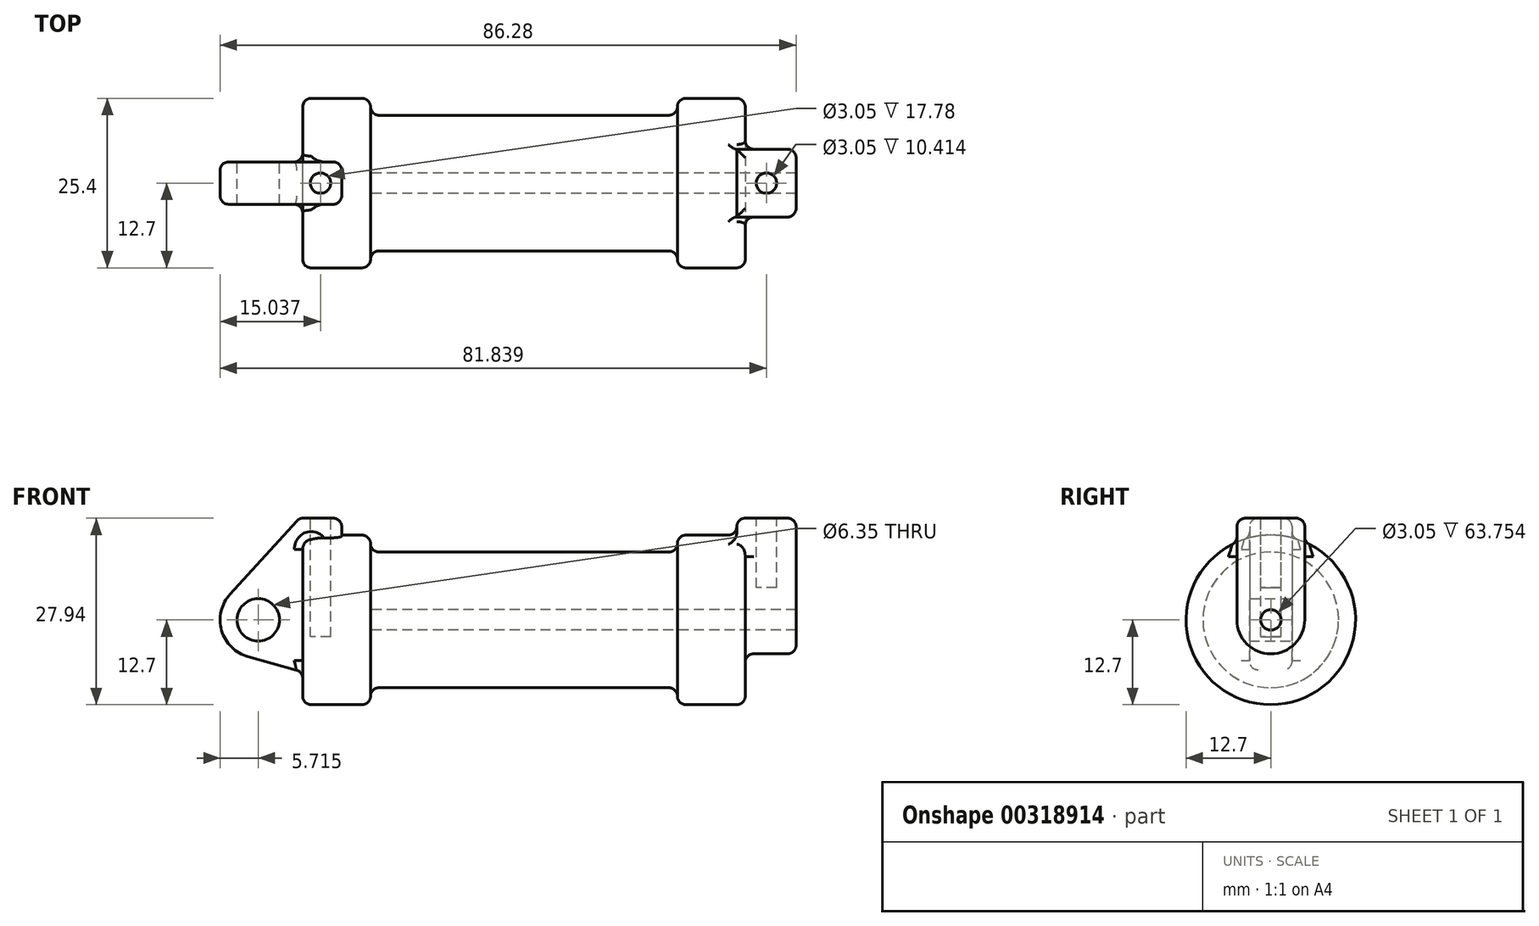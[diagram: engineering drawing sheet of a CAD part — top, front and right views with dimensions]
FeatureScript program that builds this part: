
annotation { "Feature Type Name" : "Feature", "Feature Type Description" : "" }
export const myFeature = defineFeature(function(context is Context, id is Id, definition is map)
    precondition{}
    {
        {
            var Q0;
            Q0=qCreatedBy(makeId("Front.planeOp"),FACE);
            var sketch = newSketch(context, id + "F0", { "sketchPlane" : qUnion([Q0])});
            skLineSegment(sketch, "E0", {"start": v(0, 0) * mm, "end": v(0, 12.7) * mm});
            skLineSegment(sketch, "E1", {"start": v(0, 12.7) * mm, "end": v(10.16, 12.7) * mm});
            skLineSegment(sketch, "E2", {"start": v(10.16, 12.7) * mm, "end": v(10.16, 10.16) * mm});
            skLineSegment(sketch, "E3", {"start": v(10.16, 10.16) * mm, "end": v(56.13, 10.16) * mm});
            skLineSegment(sketch, "E4", {"start": v(56.13, 10.16) * mm, "end": v(56.13, 12.7) * mm});
            skLineSegment(sketch, "E5", {"start": v(56.13, 12.7) * mm, "end": v(66.3, 12.7) * mm});
            skLineSegment(sketch, "E6", {"start": v(66.3, 12.7) * mm, "end": v(66.3, 0) * mm});
            skLineSegment(sketch, "E7", {"start": v(66.3, 0) * mm, "end": v(0, 0) * mm});
            skLineSegment(sketch, "E8", {"start": v(5.84, 15.24) * mm, "end": v(-0.5, 15.24) * mm});
            skLineSegment(sketch, "E9", {"start": v(-0.5, 15.24) * mm, "end": v(-10.88, 3.85) * mm});
            skLineSegment(sketch, "E10", {"start": v(0, 0) * mm, "end": v(-6.65, 0) * mm});
            skCircle(sketch, "E11", {"center": v(-6.65, 0) * mm, "radius": 5.72 * mm});
            skCircle(sketch, "E12", {"center": v(-6.65, 0) * mm, "radius": 3.18 * mm});
            skLineSegment(sketch, "E13", {"start": v(5.84, 15.24) * mm, "end": v(5.84, -9.4) * mm});
            skLineSegment(sketch, "E14", {"start": v(5.84, -9.4) * mm, "end": v(-8.18, -5.5) * mm});
            skSolve(sketch);
        }
        {
            var Q0;
            {var subQ0=sQuery(id+"F0.wireOp",EDGE,"E0");Q0=makeQuery(id+"F0.imprint","IMPRINT",FACE,{"disambiguationData":[TD([[makeQuery(id+"F0.imprint","IMPRINT",EDGE,{"derivedFrom":subQ0}),-1.0]])]});}
            var Q1;
            {var subQ0=sQuery(id+"F0.wireOp",EDGE,"E2");Q1=makeQuery(id+"F0.imprint","IMPRINT",FACE,{"disambiguationData":[TD([[makeQuery(id+"F0.imprint","IMPRINT",EDGE,{"derivedFrom":subQ0}),-1.0]])]});}
            var Q2;
            Q2=sQuery(id+"F0.wireOp",EDGE,"E7");
            revolve(context, id + "F1", {"entities" : qUnion([Q0, Q1]), "axis" : qUnion([Q2]), "revolveType" : RevolveType.FULL});
        }
        {
            var Q0;
            {var subQ5=sQuery(id+"F0.wireOp",EDGE,"E12");Q0=makeQuery(id+"F0.imprint","IMPRINT",FACE,{"disambiguationData":[TD([[makeQuery(id+"F0.imprint","IMPRINT",EDGE,{"derivedFrom":subQ5}),-1.0]])]});}
            var Q1;
            {var subQ0=sQuery(id+"F0.wireOp",EDGE,"E14");Q1=makeQuery(id+"F0.imprint","IMPRINT",FACE,{"disambiguationData":[TD([[makeQuery(id+"F0.imprint","IMPRINT",EDGE,{"derivedFrom":subQ0}),-1.0]])]});}
            var Q2;
            {var subQ0=sQuery(id+"F0.wireOp",EDGE,"E0");Q2=makeQuery(id+"F0.imprint","IMPRINT",FACE,{"disambiguationData":[TD([[makeQuery(id+"F0.imprint","IMPRINT",EDGE,{"derivedFrom":subQ0}),-1.0]])]});}
            var Q3;
            {var subQ1=sQuery(id+"F0.wireOp",EDGE,"E0");Q3=makeQuery(id+"F0.imprint","IMPRINT",FACE,{"disambiguationData":[TD([[makeQuery(id+"F0.imprint","IMPRINT",EDGE,{"derivedFrom":subQ1}),1.0]])]});}
            extrude(context, id + "F2", {"entities" : qUnion([Q0, Q1, Q2, Q3]), "operationType" : NewBodyOperationType.ADD, "endBound" : BoundingType.SYMMETRIC, "depth" : 6.35 * mm});
        }
        {
            var Q0;
            Q0=makeQuery(id+"F1.opRevolve","SWEPT_FACE",FACE,{"disambiguationData":[OSD([sQuery(id+"F0.wireOp",EDGE,"E6")])]});
            var sketch = newSketch(context, id + "F3", { "sketchPlane" : qUnion([Q0])});
            skCircle(sketch, "E15", {"center": v(0, 0) * mm, "radius": 1.52 * mm});
            skCircle(sketch, "E16", {"center": v(0, 0) * mm, "radius": 5.08 * mm});
            skLineSegment(sketch, "E17", {"start": v(-5.08, 0) * mm, "end": v(-5.08, 15.24) * mm});
            skLineSegment(sketch, "E18", {"start": v(-5.08, 15.24) * mm, "end": v(5.08, 15.24) * mm});
            skLineSegment(sketch, "E19", {"start": v(5.08, 15.24) * mm, "end": v(5.08, 0) * mm});
            skSolve(sketch);
        }
        {
            var Q0;
            {var subQ0=sQuery(id+"F3.wireOp",EDGE,"E18");Q0=makeQuery(id+"F3.imprint","IMPRINT",FACE,{"disambiguationData":[TD([[makeQuery(id+"F3.imprint","IMPRINT",EDGE,{"derivedFrom":subQ0}),-1.0]])]});}
            var Q1;
            {var subQ0=sQuery(id+"F3.wireOp",EDGE,"E17");var subQ1=sQuery(id+"F3.wireOp",EDGE,"E16");var subQ2=makeQuery(id+"F3.imprint","INTERSECT",VERTEX,{"derivedFrom":[subQ1,subQ0]});Q1=makeQuery(id+"F3.imprint","IMPRINT",FACE,{"disambiguationData":[TD([[makeQuery(id+"F3.imprint","IMPRINT",EDGE,{"disambiguationData":[TD([[subQ2,1.0]])],"derivedFrom":subQ1}),-1.0]])]});}
            var Q2;
            Q2=makeQuery(id+"F3.imprint","IMPRINT",FACE,{"disambiguationData":[TD([[makeQuery(id+"F3.imprint","IMPRINT",EDGE,{"derivedFrom":sQuery(id+"F3.wireOp",EDGE,"E15")}),-1.0]])]});
            extrude(context, id + "F4", {"entities" : qUnion([Q0, Q1, Q2]), "operationType" : NewBodyOperationType.ADD, "depth" : 7.62 * mm, "hasSecondDirection" : true, "secondDirectionOppositeDirection" : true, "secondDirectionDepth" : 1.27 * mm});
        }
        {
            var Q0;
            Q0=makeQuery(id+"F1.opRevolve","SWEPT_FACE",FACE,{"disambiguationData":[OSD([sQuery(id+"F0.wireOp",EDGE,"E2")])]});
            var sketch = newSketch(context, id + "F5", { "sketchPlane" : qUnion([Q0])});
            skPoint(sketch, "E20", {"position": v(0, 0) * mm});
            skSolve(sketch);
        }
        {
            var Q0;
            Q0=sQuery(id+"F5.wireOp",VERTEX,"E20");
            var Q1;
            Q1=makeQuery(id+"F1.opRevolve","SWEPT_BODY",BODY,{"disambiguationData":[OSD([sQuery(id+"F0.wireOp",EDGE,"E0"),sQuery(id+"F0.wireOp",EDGE,"E1"),sQuery(id+"F0.wireOp",EDGE,"E2"),sQuery(id+"F0.wireOp",EDGE,"E3"),sQuery(id+"F0.wireOp",EDGE,"E4"),sQuery(id+"F0.wireOp",EDGE,"E5"),sQuery(id+"F0.wireOp",EDGE,"E6"),sQuery(id+"F0.wireOp",EDGE,"E7")])]});
            hole(context, id + "F6", {"style" : HoleStyle.SIMPLE, "endStyle" : HoleEndStyle.THROUGH, "oppositeDirection" : true, "holeDiameter" : 3.05 * mm, "tappedDepth" : 12.7 * mm, "tapClearance" : 3, "locations" : qUnion([Q0]), "scope" : qUnion([Q1])});
        }
        {
            var Q0;
            Q0=makeQuery(id+"F4.opExtrude","SWEPT_FACE",FACE,{"disambiguationData":[OSD([sQuery(id+"F3.wireOp",EDGE,"E18")])]});
            var sketch = newSketch(context, id + "F7", { "sketchPlane" : qUnion([Q0])});
            skCircle(sketch, "E21", {"center": v(2.67, 0) * mm, "radius": 1.52 * mm});
            skPoint(sketch, "E21.centerSnap0", {"position": v(2.67, 3.18) * mm});
            skPoint(sketch, "E21.centerSnap1", {"position": v(5.84, 0) * mm});
            skCircle(sketch, "E22", {"center": v(69.47, 0) * mm, "radius": 1.52 * mm});
            skPoint(sketch, "E22.centerSnap0", {"position": v(69.47, 5.08) * mm});
            skPoint(sketch, "E22.centerSnap1", {"position": v(65.02, 0) * mm});
            skSolve(sketch);
        }
        {
            var Q0;
            Q0=makeQuery(id+"F7.imprint","IMPRINT",FACE,{"disambiguationData":[TD([[makeQuery(id+"F7.imprint","IMPRINT",EDGE,{"derivedFrom":sQuery(id+"F7.wireOp",EDGE,"E21")}),1.0]])]});
            extrude(context, id + "F8", {"entities" : qUnion([Q0]), "operationType" : NewBodyOperationType.REMOVE, "oppositeDirection" : true, "depth" : 17.78 * mm});
        }
        {
            var Q0;
            Q0=makeQuery(id+"F7.imprint","IMPRINT",FACE,{"disambiguationData":[TD([[makeQuery(id+"F7.imprint","IMPRINT",EDGE,{"derivedFrom":sQuery(id+"F7.wireOp",EDGE,"E22")}),1.0]])]});
            extrude(context, id + "F9", {"entities" : qUnion([Q0]), "operationType" : NewBodyOperationType.REMOVE, "oppositeDirection" : true, "depth" : 10.4 * mm});
        }
        {
            var Q0;
            Q0=makeQuery(id+"F1.opRevolve","SWEPT_EDGE",EDGE,{"disambiguationData":[OSD([sQuery(id+"F0.wireOp",EDGE,"E2"),sQuery(id+"F0.wireOp",EDGE,"E3")])]});
            var Q1;
            Q1=makeQuery(id+"F1.opRevolve","SWEPT_EDGE",EDGE,{"disambiguationData":[OSD([sQuery(id+"F0.wireOp",EDGE,"E1"),sQuery(id+"F0.wireOp",EDGE,"E2")])]});
            var Q2;
            Q2=makeQuery(id+"F1.opRevolve","SWEPT_EDGE",EDGE,{"disambiguationData":[OSD([sQuery(id+"F0.wireOp",EDGE,"E0"),sQuery(id+"F0.wireOp",EDGE,"E1")])]});
            var Q3;
            Q3=makeQuery(id+"F2.boolean.opBoolean","INTERSECT",EDGE,{"derivedFrom":[makeQuery(id+"F1.opRevolve","SWEPT_FACE",FACE,{"disambiguationData":[OSD([sQuery(id+"F0.wireOp",EDGE,"E0")])]}),makeQuery(id+"F2.opExtrude","CAP_FACE",FACE,{"disambiguationData":[OSD([sQuery(id+"F0.wireOp",EDGE,"E8"),sQuery(id+"F0.wireOp",EDGE,"E9"),sQuery(id+"F0.wireOp",EDGE,"E11"),sQuery(id+"F0.wireOp",EDGE,"E12"),sQuery(id+"F0.wireOp",EDGE,"E13"),sQuery(id+"F0.wireOp",EDGE,"E14")])],"isStart":false})]});
            var Q4;
            Q4=makeQuery(id+"F2.boolean.opBoolean","INTERSECT",EDGE,{"derivedFrom":[makeQuery(id+"F1.opRevolve","SWEPT_FACE",FACE,{"disambiguationData":[OSD([sQuery(id+"F0.wireOp",EDGE,"E0")])]}),makeQuery(id+"F2.opExtrude","SWEPT_FACE",FACE,{"disambiguationData":[OSD([sQuery(id+"F0.wireOp",EDGE,"E14")])]})]});
            var Q5;
            Q5=makeQuery(id+"F2.boolean.opBoolean","INTERSECT",EDGE,{"derivedFrom":[makeQuery(id+"F1.opRevolve","SWEPT_FACE",FACE,{"disambiguationData":[OSD([sQuery(id+"F0.wireOp",EDGE,"E0")])]}),makeQuery(id+"F2.opExtrude","CAP_FACE",FACE,{"disambiguationData":[OSD([sQuery(id+"F0.wireOp",EDGE,"E8"),sQuery(id+"F0.wireOp",EDGE,"E9"),sQuery(id+"F0.wireOp",EDGE,"E11"),sQuery(id+"F0.wireOp",EDGE,"E12"),sQuery(id+"F0.wireOp",EDGE,"E13"),sQuery(id+"F0.wireOp",EDGE,"E14")])],"isStart":true})]});
            var Q6;
            Q6=makeQuery(id+"F2.opExtrude","CAP_EDGE",EDGE,{"disambiguationData":[OSD([sQuery(id+"F0.wireOp",EDGE,"E14")])],"isStart":true});
            var Q7;
            Q7=makeQuery(id+"F2.opExtrude","CAP_EDGE",EDGE,{"disambiguationData":[OSD([sQuery(id+"F0.wireOp",EDGE,"E14")])],"isStart":false});
            var Q8;
            Q8=makeQuery(id+"F2.opExtrude","CAP_EDGE",EDGE,{"disambiguationData":[OSD([sQuery(id+"F0.wireOp",EDGE,"E13")])],"isStart":false});
            var Q9;
            Q9=makeQuery(id+"F2.opExtrude","CAP_EDGE",EDGE,{"disambiguationData":[OSD([sQuery(id+"F0.wireOp",EDGE,"E13")])],"isStart":true});
            var Q10;
            Q10=makeQuery(id+"F2.opExtrude","SWEPT_EDGE",EDGE,{"disambiguationData":[OSD([sQuery(id+"F0.wireOp",EDGE,"E8"),sQuery(id+"F0.wireOp",EDGE,"E9")])]});
            var Q11;
            Q11=makeQuery(id+"F2.opExtrude","SWEPT_EDGE",EDGE,{"disambiguationData":[OSD([sQuery(id+"F0.wireOp",EDGE,"E8"),sQuery(id+"F0.wireOp",EDGE,"E13")])]});
            var Q12;
            Q12=makeQuery(id+"F2.opExtrude","CAP_EDGE",EDGE,{"disambiguationData":[OSD([sQuery(id+"F0.wireOp",EDGE,"E8")])],"isStart":false});
            var Q13;
            Q13=makeQuery(id+"F2.opExtrude","CAP_EDGE",EDGE,{"disambiguationData":[OSD([sQuery(id+"F0.wireOp",EDGE,"E8")])],"isStart":true});
            fillet(context, id + "F10", {"entities" : qUnion([Q0, Q1, Q2, Q3, Q4, Q5, Q6, Q7, Q8, Q9, Q10, Q11, Q12, Q13]), "radius" : 1.27 * mm, "tangentPropagation" : true, "allowEdgeOverflow" : false});
        }
        {
            var Q0;
            Q0=makeQuery(id+"F1.opRevolve","SWEPT_EDGE",EDGE,{"disambiguationData":[OSD([sQuery(id+"F0.wireOp",EDGE,"E3"),sQuery(id+"F0.wireOp",EDGE,"E4")])]});
            var Q1;
            Q1=makeQuery(id+"F1.opRevolve","SWEPT_EDGE",EDGE,{"disambiguationData":[OSD([sQuery(id+"F0.wireOp",EDGE,"E4"),sQuery(id+"F0.wireOp",EDGE,"E5")])]});
            var Q2;
            Q2=makeQuery(id+"F1.opRevolve","SWEPT_EDGE",EDGE,{"disambiguationData":[OSD([sQuery(id+"F0.wireOp",EDGE,"E5"),sQuery(id+"F0.wireOp",EDGE,"E6")])]});
            fillet(context, id + "F11", {"entities" : qUnion([Q0, Q1, Q2]), "radius" : 1.27 * mm, "tangentPropagation" : true, "allowEdgeOverflow" : false});
        }
        {
            var Q0;
            Q0=makeQuery(id+"F4.boolean.opBoolean","INTERSECT",EDGE,{"derivedFrom":[makeQuery(id+"F1.opRevolve","SWEPT_FACE",FACE,{"disambiguationData":[OSD([sQuery(id+"F0.wireOp",EDGE,"E5")])]}),makeQuery(id+"F4.opExtrude","CAP_FACE",FACE,{"disambiguationData":[OSD([sQuery(id+"F3.wireOp",EDGE,"E15"),sQuery(id+"F3.wireOp",EDGE,"E16"),sQuery(id+"F3.wireOp",EDGE,"E17"),sQuery(id+"F3.wireOp",EDGE,"E18"),sQuery(id+"F3.wireOp",EDGE,"E19")])],"isStart":true})]});
            var Q1;
            Q1=makeQuery(id+"F4.opExtrude","CAP_EDGE",EDGE,{"disambiguationData":[OSD([sQuery(id+"F3.wireOp",EDGE,"E18")])],"isStart":true});
            var Q2;
            Q2=makeQuery(id+"F4.opExtrude","SWEPT_EDGE",EDGE,{"disambiguationData":[OSD([sQuery(id+"F3.wireOp",EDGE,"E17"),sQuery(id+"F3.wireOp",EDGE,"E18")])]});
            var Q3;
            Q3=makeQuery(id+"F4.opExtrude","CAP_EDGE",EDGE,{"disambiguationData":[OSD([sQuery(id+"F3.wireOp",EDGE,"E18")])],"isStart":false});
            var Q4;
            Q4=makeQuery(id+"F4.opExtrude","SWEPT_EDGE",EDGE,{"disambiguationData":[OSD([sQuery(id+"F3.wireOp",EDGE,"E18"),sQuery(id+"F3.wireOp",EDGE,"E19")])]});
            var Q5;
            Q5=makeQuery(id+"F4.boolean.opBoolean","INTERSECT",EDGE,{"derivedFrom":[makeQuery(id+"F1.opRevolve","SWEPT_FACE",FACE,{"disambiguationData":[OSD([sQuery(id+"F0.wireOp",EDGE,"E6")])]}),makeQuery(id+"F4.opExtrude","SWEPT_FACE",FACE,{"disambiguationData":[OSD([sQuery(id+"F3.wireOp",EDGE,"E17")])]})]});
            var Q6;
            Q6=makeQuery(id+"F4.opExtrude","CAP_EDGE",EDGE,{"disambiguationData":[OSD([sQuery(id+"F3.wireOp",EDGE,"E19")])],"isStart":false});
            fillet(context, id + "F12", {"entities" : qUnion([Q0, Q1, Q2, Q3, Q4, Q5, Q6]), "radius" : 1.27 * mm, "tangentPropagation" : true, "allowEdgeOverflow" : false});
        }
    });
